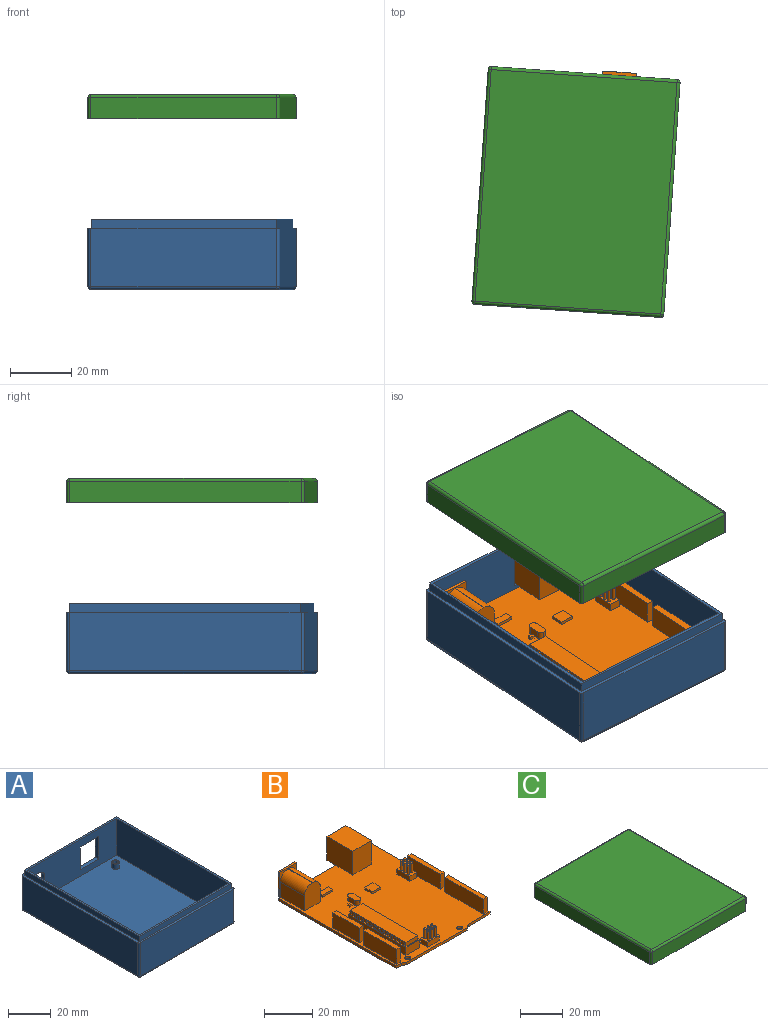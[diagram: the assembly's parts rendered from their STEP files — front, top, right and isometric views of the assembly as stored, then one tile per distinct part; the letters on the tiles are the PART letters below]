
ASSEMBLY  parts=3 mates=4
PART A: 49 faces, bbox 63x78x23 mm
  f0: plane 78x63mm, normal (0,0,1), area 294.3mm2, adj f2,f3,f4,f5,f32,f33,f34,f35
  f1: plane 59x21mm, normal (0,-1,0), area 1031.5mm2, adj f8,f9,f10,f27,f28,f29,f30,f31
  f2: plane 76x19mm, normal (1,0,0), area 1444mm2, adj f0,f39,f45,f48
  f3: plane 61x19mm, normal (0,-1,0), area 1159mm2, adj f0,f42,f46,f48
  f4: plane 76x19mm, normal (-1,0,0), area 1444mm2, adj f0,f37,f41,f42
  f5: plane 61x19mm, normal (0,1,0), area 951.5mm2, adj f0,f27,f28,f29,f30,f31,f37,f39
  f6: plane 76x61mm, normal (0,0,-1), area 4636mm2, adj f40,f41,f45,f46
  f7: plane 59x21mm, normal (0,1,0), area 1239mm2, adj f8,f9,f10,f36
  f8: plane 74x21mm, normal (-1,0,0), area 1554mm2, adj f1,f7,f10,f36
  f9: plane 74x21mm, normal (1,0,0), area 1554mm2, adj f1,f7,f10,f36
  f10: plane 74x59mm, normal (0,0,1), area 4327.5mm2, adj f1,f7,f8,f9,f12,f16,f20,f24
  f11: cylinder r=1.25mm len=3mm, axis (0,0,-1), area 23.6mm2, adj f13,f14
  f12: cylinder r=1.75mm len=3.5mm, axis (0,0,-1), area 33mm2, adj f10,f13
  f13: plane 3.5x3.5mm, normal (0,0,1), area 4.7mm2, adj f11,f12
  f14: plane 2.5x2.5mm, normal (0,0,1), area 4.9mm2, adj f11
  f15: cylinder r=1.25mm len=3mm, axis (0,0,-1), area 23.6mm2, adj f17,f18
  f16: cylinder r=1.75mm len=3.5mm, axis (0,0,-1), area 33mm2, adj f10,f17
  f17: plane 3.5x3.5mm, normal (0,0,1), area 4.7mm2, adj f15,f16
  f18: plane 2.5x2.5mm, normal (0,0,1), area 4.9mm2, adj f15
  f19: cylinder r=1.25mm len=3mm, axis (0,0,-1), area 23.6mm2, adj f21,f22
  f20: cylinder r=1.75mm len=3.5mm, axis (0,0,-1), area 33mm2, adj f10,f21
  f21: plane 3.5x3.5mm, normal (0,0,1), area 4.7mm2, adj f19,f20
  f22: plane 2.5x2.5mm, normal (0,0,1), area 4.9mm2, adj f19
  f23: cylinder r=1.25mm len=3mm, axis (0,0,-1), area 23.6mm2, adj f25,f26
  f24: cylinder r=1.75mm len=3.5mm, axis (0,0,-1), area 33mm2, adj f10,f25
  f25: plane 3.5x3.5mm, normal (0,0,1), area 4.7mm2, adj f23,f24
  f26: plane 2.5x2.5mm, normal (0,0,1), area 4.9mm2, adj f23
  f27: plane 13x2mm, normal (-1,0,0), area 26mm2, adj f1,f5,f28,f30
  f28: plane 12.11x2mm, normal (0,0,1), area 24.2mm2, adj f1,f5,f27,f29
  f29: plane 13x2mm, normal (1,0,0), area 26mm2, adj f1,f5,f28,f30
  f30: plane 12.11x2mm, normal (0,0,-1), area 24.2mm2, adj f1,f5,f27,f29
  f31: cylinder r=3.99mm len=7.98mm, axis (0,1,0), area 50.2mm2, adj f1,f5
  f32: plane 75.88x3mm, normal (1,0,0), area 227.6mm2, adj f0,f33,f35,f36
  f33: plane 60.88x3mm, normal (0,1,0), area 182.6mm2, adj f0,f32,f34,f36
  f34: plane 75.88x3mm, normal (-1,0,0), area 227.6mm2, adj f0,f33,f35,f36
  f35: plane 60.88x3mm, normal (0,-1,0), area 182.6mm2, adj f0,f32,f34,f36
  f36: plane 75.88x60.88mm, normal (0,0,1), area 252.9mm2, adj f1,f7,f8,f9,f32,f33,f34,f35
  f37: cylinder r=1mm len=19mm, axis (0,0,1), area 29.8mm2, adj f0,f4,f5,f38
  f38: sphere r=1mm, area 1.6mm2, adj f37,f40,f41
  f39: cylinder r=1mm len=19mm, axis (0,0,-1), area 29.8mm2, adj f0,f2,f5,f43
  f40: cylinder r=1mm len=61mm, axis (-1,0,0), area 95.8mm2, adj f5,f6,f38,f43
  f41: cylinder r=1mm len=76mm, axis (0,-1,0), area 119.4mm2, adj f4,f6,f38,f44
  f42: cylinder r=1mm len=19mm, axis (0,0,-1), area 29.8mm2, adj f0,f3,f4,f44
  f43: sphere r=1mm, area 1.6mm2, adj f39,f40,f45
  f44: sphere r=1mm, area 1.6mm2, adj f41,f42,f46
  f45: cylinder r=1mm len=76mm, axis (0,1,0), area 119.4mm2, adj f2,f6,f43,f47
  f46: cylinder r=1mm len=61mm, axis (1,0,0), area 95.8mm2, adj f3,f6,f44,f47
  f47: sphere r=1mm, area 1.6mm2, adj f45,f46,f48
  f48: cylinder r=1mm len=19mm, axis (0,0,1), area 29.8mm2, adj f0,f2,f3,f47
PART B: 244 faces, bbox 55x75.2x13.8 mm
  f0: plane 7x4mm, normal (0,0,1), area 23.3mm2, adj f194,f195,f196,f197,f226,f227,f228,f229
  f1: plane 7.5x4mm, normal (0,0,1), area 25.3mm2, adj f190,f191,f192,f193,f220,f221,f222,f223
  f2: plane 70x55mm, normal (0,0,1), area 3025.5mm2, adj f49,f50,f51,f52,f54,f55,f56,f57
  f3: plane 8.98x8.63mm, normal (0,1,0), area 52mm2, adj f179,f180,f181,f182,f183,f184,f185,f186
  f4: plane 1.5x0.4mm, normal (0,1,0), area 0.6mm2, adj f6,f46,f48,f178
  f5: plane 1.5x0.4mm, normal (0,-1,0), area 0.6mm2, adj f6,f46,f48,f178
  f6: plane 0.75x0.4mm, normal (0,0,1), area 0.3mm2, adj f4,f5,f46,f178
  f7: plane 1.5x0.4mm, normal (0,1,0), area 0.6mm2, adj f9,f46,f48,f177
  f8: plane 1.5x0.4mm, normal (0,-1,0), area 0.6mm2, adj f9,f46,f48,f177
  f9: plane 0.75x0.4mm, normal (0,0,1), area 0.3mm2, adj f7,f8,f46,f177
  f10: plane 1.5x0.4mm, normal (0,1,0), area 0.6mm2, adj f12,f46,f48,f176
  f11: plane 1.5x0.4mm, normal (0,-1,0), area 0.6mm2, adj f12,f46,f48,f176
  f12: plane 0.75x0.4mm, normal (0,0,1), area 0.3mm2, adj f10,f11,f46,f176
  f13: plane 1.5x0.4mm, normal (0,1,0), area 0.6mm2, adj f15,f46,f48,f175
  f14: plane 1.5x0.4mm, normal (0,-1,0), area 0.6mm2, adj f15,f46,f48,f175
  f15: plane 0.75x0.4mm, normal (0,0,1), area 0.3mm2, adj f13,f14,f46,f175
  f16: plane 1.5x0.4mm, normal (0,1,0), area 0.6mm2, adj f18,f46,f48,f174
  f17: plane 1.5x0.4mm, normal (0,-1,0), area 0.6mm2, adj f18,f46,f48,f174
  f18: plane 0.75x0.4mm, normal (0,0,1), area 0.3mm2, adj f16,f17,f46,f174
  f19: plane 1.5x0.4mm, normal (0,1,0), area 0.6mm2, adj f21,f46,f48,f173
  f20: plane 1.5x0.4mm, normal (0,-1,0), area 0.6mm2, adj f21,f46,f48,f173
  f21: plane 0.75x0.4mm, normal (0,0,1), area 0.3mm2, adj f19,f20,f46,f173
  f22: plane 1.5x0.4mm, normal (0,1,0), area 0.6mm2, adj f24,f46,f48,f172
  f23: plane 1.5x0.4mm, normal (0,-1,0), area 0.6mm2, adj f24,f46,f48,f172
  f24: plane 0.75x0.4mm, normal (0,0,1), area 0.3mm2, adj f22,f23,f46,f172
  f25: plane 1.5x0.4mm, normal (0,1,0), area 0.6mm2, adj f27,f46,f48,f171
  f26: plane 1.5x0.4mm, normal (0,-1,0), area 0.6mm2, adj f27,f46,f48,f171
  f27: plane 0.75x0.4mm, normal (0,0,1), area 0.3mm2, adj f25,f26,f46,f171
  f28: plane 1.5x0.4mm, normal (0,1,0), area 0.6mm2, adj f30,f46,f48,f170
  f29: plane 1.5x0.4mm, normal (0,-1,0), area 0.6mm2, adj f30,f46,f48,f170
  f30: plane 0.75x0.4mm, normal (0,0,1), area 0.3mm2, adj f28,f29,f46,f170
  f31: plane 1.5x0.4mm, normal (0,1,0), area 0.6mm2, adj f33,f46,f48,f169
  f32: plane 1.5x0.4mm, normal (0,-1,0), area 0.6mm2, adj f33,f46,f48,f169
  f33: plane 0.75x0.4mm, normal (0,0,1), area 0.3mm2, adj f31,f32,f46,f169
  f34: plane 1.5x0.4mm, normal (0,1,0), area 0.6mm2, adj f36,f46,f48,f168
  f35: plane 1.5x0.4mm, normal (0,-1,0), area 0.6mm2, adj f36,f46,f48,f168
  f36: plane 0.75x0.4mm, normal (0,0,1), area 0.3mm2, adj f34,f35,f46,f168
  f37: plane 1.5x0.4mm, normal (0,1,0), area 0.6mm2, adj f39,f46,f48,f167
  f38: plane 1.5x0.4mm, normal (0,-1,0), area 0.6mm2, adj f39,f46,f48,f167
  f39: plane 0.75x0.4mm, normal (0,0,1), area 0.3mm2, adj f37,f38,f46,f167
  f40: plane 1.5x0.4mm, normal (0,1,0), area 0.6mm2, adj f42,f46,f48,f166
  f41: plane 1.5x0.4mm, normal (0,-1,0), area 0.6mm2, adj f42,f46,f48,f166
  f42: plane 0.75x0.4mm, normal (0,0,1), area 0.3mm2, adj f40,f41,f46,f166
  f43: plane 1.5x0.4mm, normal (0,1,0), area 0.6mm2, adj f45,f46,f48,f165
  f44: plane 1.5x0.4mm, normal (0,-1,0), area 0.6mm2, adj f45,f46,f48,f165
  f45: plane 0.75x0.4mm, normal (0,0,1), area 0.3mm2, adj f43,f44,f46,f165
  f46: plane 32.63x2mm, normal (1,0,0), area 49.5mm2, adj f4,f5,f6,f7,f8,f9,f10,f11
  f47: plane 32.63x2mm, normal (-1,0,0), area 49.5mm2, adj f48,f106,f107,f108,f109,f110,f111,f112
  f48: plane 33.63x7.95mm, normal (0,0,1), area 32.2mm2, adj f4,f5,f7,f8,f10,f11,f13,f14
  f49: plane 33.63x4mm, normal (-1,0,0), area 134.5mm2, adj f2,f48,f50,f52
  f50: plane 7.95x4mm, normal (0,-1,0), area 31.8mm2, adj f2,f48,f49,f51
  f51: plane 33.63x4mm, normal (1,0,0), area 134.5mm2, adj f2,f48,f50,f52
  f52: plane 7.95x4mm, normal (0,1,0), area 31.8mm2, adj f2,f48,f49,f51
  f53: plane 6.98x6.98mm, normal (0,1,0), area 37.5mm2, adj f103,f104
  f54: plane 68.67x1.25mm, normal (1,0,0), area 85.8mm2, adj f2,f55,f58,f95
  f55: plane 55x1.25mm, normal (0,1,0), area 68.8mm2, adj f2,f54,f56,f58,f79,f84
  f56: plane 68.67x1.25mm, normal (-1,0,0), area 85.8mm2, adj f2,f55,f58,f92
  f57: plane 35.3x1.25mm, normal (0,-1,0), area 44.1mm2, adj f2,f58,f93,f94
  f58: plane 70x55mm, normal (0,0,-1), area 3816.6mm2, adj f54,f55,f56,f57,f92,f93,f94,f95
  f59: plane 7.5x2.22mm, normal (0,-1,0), area 16.7mm2, adj f2,f60,f62,f63
  f60: plane 22.58x7.5mm, normal (1,0,0), area 169.3mm2, adj f2,f59,f61,f63
  f61: plane 7.5x2.22mm, normal (0,1,0), area 16.7mm2, adj f2,f60,f62,f63
  f62: plane 22.58x7.5mm, normal (-1,0,0), area 169.3mm2, adj f2,f59,f61,f63
  f63: plane 22.58x2.22mm, normal (0,0,1), area 50.1mm2, adj f59,f60,f61,f62
  f64: plane 19.27x7.5mm, normal (-1,0,0), area 144.5mm2, adj f2,f65,f67,f68
  f65: plane 7.5x2.22mm, normal (0,-1,0), area 16.7mm2, adj f2,f64,f66,f68
  f66: plane 19.27x7.5mm, normal (1,0,0), area 144.5mm2, adj f2,f65,f67,f68
  f67: plane 7.5x2.22mm, normal (0,1,0), area 16.7mm2, adj f2,f64,f66,f68
  f68: plane 19.27x2.22mm, normal (0,0,1), area 42.8mm2, adj f64,f65,f66,f67
  f69: plane 19.1x7.5mm, normal (-1,0,0), area 143.2mm2, adj f2,f70,f72,f73
  f70: plane 7.5x2.22mm, normal (0,-1,0), area 16.7mm2, adj f2,f69,f71,f73
  f71: plane 19.1x7.5mm, normal (1,0,0), area 143.2mm2, adj f2,f70,f72,f73
  f72: plane 7.5x2.22mm, normal (0,1,0), area 16.7mm2, adj f2,f69,f71,f73
  f73: plane 19.1x2.22mm, normal (0,0,1), area 42.4mm2, adj f69,f70,f71,f72
  f74: plane 15.53x7.5mm, normal (1,0,0), area 116.5mm2, adj f2,f75,f77,f78
  f75: plane 7.5x2.22mm, normal (0,1,0), area 16.7mm2, adj f2,f74,f76,f78
  f76: plane 15.53x7.5mm, normal (-1,0,0), area 116.5mm2, adj f2,f75,f77,f78
  f77: plane 7.5x2.22mm, normal (0,-1,0), area 16.7mm2, adj f2,f74,f76,f78
  f78: plane 15.53x2.22mm, normal (0,0,1), area 34.5mm2, adj f74,f75,f76,f77
  f79: plane 9.89x1.2mm, normal (0,0,-1), area 11.7mm2, adj f55,f80,f82,f98,f99,f101,f102
  f80: plane 14.15x7.5mm, normal (-1,0,0), area 106.1mm2, adj f2,f79,f81,f90,f98
  f81: plane 12x9.24mm, normal (0,-1,0), area 102.2mm2, adj f2,f80,f82,f83,f90,f91
  f82: plane 14.15x7.5mm, normal (1,0,0), area 106.1mm2, adj f2,f79,f81,f91,f98
  f83: plane 14.15x0.24mm, normal (0,0,1), area 3.4mm2, adj f81,f90,f91,f98
  f84: plane 11.11x5.16mm, normal (0,0,-1), area 57.3mm2, adj f55,f85,f87,f88
  f85: plane 15.05x12mm, normal (-1,0,0), area 180.6mm2, adj f2,f84,f86,f88,f89
  f86: plane 12x11.11mm, normal (0,-1,0), area 133.3mm2, adj f2,f85,f87,f89
  f87: plane 15.05x12mm, normal (1,0,0), area 180.6mm2, adj f2,f84,f86,f88,f89
  f88: plane 12x11.11mm, normal (0,1,0), area 60.1mm2, adj f84,f85,f87,f89,f179,f180,f181,f182
  f89: plane 15.05x11.11mm, normal (0,0,1), area 167.2mm2, adj f85,f86,f87,f88
  f90: cylinder r=4.5mm len=14.15mm, axis (0,1,0), area 100mm2, adj f80,f81,f83,f98
  f91: cylinder r=4.5mm len=14.15mm, axis (0,-1,0), area 100mm2, adj f81,f82,f83,f98
  f92: plane 2.98x1.25mm, normal (0,-1,0), area 3.7mm2, adj f2,f56,f58,f93
  f93: plane 2.01x1.33mm, normal (-0.55,-0.83,0), area 3mm2, adj f2,f57,f58,f92
  f94: plane 2.01x1.33mm, normal (0.55,-0.83,0), area 3mm2, adj f2,f57,f58,f95
  f95: plane 12.71x1.25mm, normal (0,-1,0), area 15.9mm2, adj f2,f54,f58,f94
  f96: cylinder r=1.25mm len=2.5mm, axis (0,0,1), area 9.8mm2, adj f2,f58
  f97: cylinder r=1.25mm len=2.5mm, axis (0,0,1), area 9.8mm2, adj f2,f58
  f98: plane 12.57x9.89mm, normal (0,-1,0), area 22.1mm2, adj f79,f80,f82,f83,f90,f91,f99,f100
  f99: plane 12.57x1mm, normal (-1,0,0), area 12.6mm2, adj f79,f98,f100,f102
  f100: plane 9.89x1mm, normal (0,0,1), area 9.9mm2, adj f98,f99,f101,f102
  f101: plane 12.57x1mm, normal (1,0,0), area 12.6mm2, adj f79,f98,f100,f102
  f102: plane 12.57x9.89mm, normal (0,1,0), area 86mm2, adj f79,f99,f100,f101,f103
  f103: cylinder r=3.49mm len=12mm, axis (0,1,0), area 263.3mm2, adj f53,f102
  f104: cylinder r=0.5mm len=8mm, axis (0,-1,0), area 25.1mm2, adj f53,f105
  f105: plane 1x1mm, normal (0,1,0), area 0.8mm2, adj f104
  f106: plane 6.95x2mm, normal (0,1,0), area 13.9mm2, adj f46,f47,f48,f108
  f107: plane 6.95x2mm, normal (0,-1,0), area 13.9mm2, adj f46,f47,f48,f108
  f108: plane 32.63x6.95mm, normal (0,0,1), area 226.7mm2, adj f46,f47,f106,f107
  f109: plane 1.5x0.4mm, normal (0,1,0), area 0.6mm2, adj f47,f48,f111,f164
  f110: plane 1.5x0.4mm, normal (0,-1,0), area 0.6mm2, adj f47,f48,f111,f164
  f111: plane 0.75x0.4mm, normal (0,0,1), area 0.3mm2, adj f47,f109,f110,f164
  f112: plane 1.5x0.4mm, normal (0,1,0), area 0.6mm2, adj f47,f48,f114,f163
  f113: plane 1.5x0.4mm, normal (0,-1,0), area 0.6mm2, adj f47,f48,f114,f163
  f114: plane 0.75x0.4mm, normal (0,0,1), area 0.3mm2, adj f47,f112,f113,f163
  f115: plane 1.5x0.4mm, normal (0,1,0), area 0.6mm2, adj f47,f48,f117,f162
  f116: plane 1.5x0.4mm, normal (0,-1,0), area 0.6mm2, adj f47,f48,f117,f162
  f117: plane 0.75x0.4mm, normal (0,0,1), area 0.3mm2, adj f47,f115,f116,f162
  f118: plane 1.5x0.4mm, normal (0,1,0), area 0.6mm2, adj f47,f48,f120,f161
  f119: plane 1.5x0.4mm, normal (0,-1,0), area 0.6mm2, adj f47,f48,f120,f161
  f120: plane 0.75x0.4mm, normal (0,0,1), area 0.3mm2, adj f47,f118,f119,f161
  f121: plane 1.5x0.4mm, normal (0,1,0), area 0.6mm2, adj f47,f48,f123,f160
  f122: plane 1.5x0.4mm, normal (0,-1,0), area 0.6mm2, adj f47,f48,f123,f160
  f123: plane 0.75x0.4mm, normal (0,0,1), area 0.3mm2, adj f47,f121,f122,f160
  f124: plane 1.5x0.4mm, normal (0,1,0), area 0.6mm2, adj f47,f48,f126,f159
  f125: plane 1.5x0.4mm, normal (0,-1,0), area 0.6mm2, adj f47,f48,f126,f159
  f126: plane 0.75x0.4mm, normal (0,0,1), area 0.3mm2, adj f47,f124,f125,f159
  f127: plane 1.5x0.4mm, normal (0,1,0), area 0.6mm2, adj f47,f48,f129,f158
  f128: plane 1.5x0.4mm, normal (0,-1,0), area 0.6mm2, adj f47,f48,f129,f158
  f129: plane 0.75x0.4mm, normal (0,0,1), area 0.3mm2, adj f47,f127,f128,f158
  f130: plane 1.5x0.4mm, normal (0,1,0), area 0.6mm2, adj f47,f48,f132,f157
  f131: plane 1.5x0.4mm, normal (0,-1,0), area 0.6mm2, adj f47,f48,f132,f157
  f132: plane 0.75x0.4mm, normal (0,0,1), area 0.3mm2, adj f47,f130,f131,f157
  f133: plane 1.5x0.4mm, normal (0,1,0), area 0.6mm2, adj f47,f48,f135,f156
  f134: plane 1.5x0.4mm, normal (0,-1,0), area 0.6mm2, adj f47,f48,f135,f156
  f135: plane 0.75x0.4mm, normal (0,0,1), area 0.3mm2, adj f47,f133,f134,f156
  f136: plane 1.5x0.4mm, normal (0,1,0), area 0.6mm2, adj f47,f48,f138,f155
  f137: plane 1.5x0.4mm, normal (0,-1,0), area 0.6mm2, adj f47,f48,f138,f155
  f138: plane 0.75x0.4mm, normal (0,0,1), area 0.3mm2, adj f47,f136,f137,f155
  f139: plane 1.5x0.4mm, normal (0,1,0), area 0.6mm2, adj f47,f48,f141,f154
  f140: plane 1.5x0.4mm, normal (0,-1,0), area 0.6mm2, adj f47,f48,f141,f154
  f141: plane 0.75x0.4mm, normal (0,0,1), area 0.3mm2, adj f47,f139,f140,f154
  f142: plane 1.5x0.4mm, normal (0,1,0), area 0.6mm2, adj f47,f48,f144,f153
  f143: plane 1.5x0.4mm, normal (0,-1,0), area 0.6mm2, adj f47,f48,f144,f153
  f144: plane 0.75x0.4mm, normal (0,0,1), area 0.3mm2, adj f47,f142,f143,f153
  f145: plane 1.5x0.4mm, normal (0,1,0), area 0.6mm2, adj f47,f48,f147,f152
  f146: plane 1.5x0.4mm, normal (0,-1,0), area 0.6mm2, adj f47,f48,f147,f152
  f147: plane 0.75x0.4mm, normal (0,0,1), area 0.3mm2, adj f47,f145,f146,f152
  f148: plane 1.5x0.4mm, normal (0,1,0), area 0.6mm2, adj f47,f48,f150,f151
  f149: plane 1.5x0.4mm, normal (0,-1,0), area 0.6mm2, adj f47,f48,f150,f151
  f150: plane 0.75x0.4mm, normal (0,0,1), area 0.3mm2, adj f47,f148,f149,f151
  f151: plane 1.5x0.75mm, normal (-1,0,0), area 1.1mm2, adj f48,f148,f149,f150
  f152: plane 1.5x0.75mm, normal (-1,0,0), area 1.1mm2, adj f48,f145,f146,f147
  f153: plane 1.5x0.75mm, normal (-1,0,0), area 1.1mm2, adj f48,f142,f143,f144
  f154: plane 1.5x0.75mm, normal (-1,0,0), area 1.1mm2, adj f48,f139,f140,f141
  f155: plane 1.5x0.75mm, normal (-1,0,0), area 1.1mm2, adj f48,f136,f137,f138
  f156: plane 1.5x0.75mm, normal (-1,0,0), area 1.1mm2, adj f48,f133,f134,f135
  f157: plane 1.5x0.75mm, normal (-1,0,0), area 1.1mm2, adj f48,f130,f131,f132
  f158: plane 1.5x0.75mm, normal (-1,0,0), area 1.1mm2, adj f48,f127,f128,f129
  f159: plane 1.5x0.75mm, normal (-1,0,0), area 1.1mm2, adj f48,f124,f125,f126
  f160: plane 1.5x0.75mm, normal (-1,0,0), area 1.1mm2, adj f48,f121,f122,f123
  f161: plane 1.5x0.75mm, normal (-1,0,0), area 1.1mm2, adj f48,f118,f119,f120
  f162: plane 1.5x0.75mm, normal (-1,0,0), area 1.1mm2, adj f48,f115,f116,f117
  f163: plane 1.5x0.75mm, normal (-1,0,0), area 1.1mm2, adj f48,f112,f113,f114
  f164: plane 1.5x0.75mm, normal (-1,0,0), area 1.1mm2, adj f48,f109,f110,f111
  f165: plane 1.5x0.75mm, normal (1,0,0), area 1.1mm2, adj f43,f44,f45,f48
  f166: plane 1.5x0.75mm, normal (1,0,0), area 1.1mm2, adj f40,f41,f42,f48
  f167: plane 1.5x0.75mm, normal (1,0,0), area 1.1mm2, adj f37,f38,f39,f48
  f168: plane 1.5x0.75mm, normal (1,0,0), area 1.1mm2, adj f34,f35,f36,f48
  f169: plane 1.5x0.75mm, normal (1,0,0), area 1.1mm2, adj f31,f32,f33,f48
  f170: plane 1.5x0.75mm, normal (1,0,0), area 1.1mm2, adj f28,f29,f30,f48
  f171: plane 1.5x0.75mm, normal (1,0,0), area 1.1mm2, adj f25,f26,f27,f48
  f172: plane 1.5x0.75mm, normal (1,0,0), area 1.1mm2, adj f22,f23,f24,f48
  f173: plane 1.5x0.75mm, normal (1,0,0), area 1.1mm2, adj f19,f20,f21,f48
  f174: plane 1.5x0.75mm, normal (1,0,0), area 1.1mm2, adj f16,f17,f18,f48
  f175: plane 1.5x0.75mm, normal (1,0,0), area 1.1mm2, adj f13,f14,f15,f48
  f176: plane 1.5x0.75mm, normal (1,0,0), area 1.1mm2, adj f10,f11,f12,f48
  f177: plane 1.5x0.75mm, normal (1,0,0), area 1.1mm2, adj f7,f8,f9,f48
  f178: plane 1.5x0.75mm, normal (1,0,0), area 1.1mm2, adj f4,f5,f6,f48
  f179: plane 10x6.73mm, normal (1,0,0), area 67.3mm2, adj f3,f88,f180,f184
  f180: plane 10x8.63mm, normal (0,0,1), area 86.3mm2, adj f3,f88,f179,f181
  f181: plane 10x6.73mm, normal (-1,0,0), area 67.3mm2, adj f3,f88,f180,f182
  f182: plane 10x2.24mm, normal (-0.76,0,-0.65), area 29.4mm2, adj f3,f88,f181,f183
  f183: plane 10x4.83mm, normal (0,0,-1), area 48.3mm2, adj f3,f88,f182,f184
  f184: plane 10x2.24mm, normal (0.76,0,-0.65), area 29.4mm2, adj f3,f88,f179,f183
  f185: plane 8x3.45mm, normal (-1,0,0), area 27.6mm2, adj f3,f186,f188,f189
  f186: plane 8x6.13mm, normal (0,0,1), area 49mm2, adj f3,f185,f187,f189
  f187: plane 8x3.45mm, normal (1,0,0), area 27.6mm2, adj f3,f186,f188,f189
  f188: plane 8x6.13mm, normal (0,0,-1), area 49mm2, adj f3,f185,f187,f189
  f189: plane 6.13x3.45mm, normal (0,1,0), area 21.2mm2, adj f185,f186,f187,f188
  f190: plane 7.5x2.5mm, normal (-1,0,0), area 18.7mm2, adj f1,f2,f191,f193
  f191: plane 4x2.5mm, normal (0,-1,0), area 10mm2, adj f1,f2,f190,f192
  f192: plane 7.5x2.5mm, normal (1,0,0), area 18.7mm2, adj f1,f2,f191,f193
  f193: plane 4x2.5mm, normal (0,1,0), area 10mm2, adj f1,f2,f190,f192
  f194: plane 4x2.5mm, normal (-1,0,0), area 10mm2, adj f0,f2,f195,f197
  f195: plane 7x2.5mm, normal (0,-1,0), area 17.5mm2, adj f0,f2,f194,f196
  f196: plane 4x2.5mm, normal (1,0,0), area 10mm2, adj f0,f2,f195,f197
  f197: plane 7x2.5mm, normal (0,1,0), area 17.5mm2, adj f0,f2,f194,f196
  f198: plane 3.5x2.5mm, normal (-1,0,0), area 8.8mm2, adj f2,f200,f201,f203
  f199: plane 3.5x2.5mm, normal (1,0,0), area 8.8mm2, adj f2,f200,f202,f204
  f200: plane 6.5x3mm, normal (0,0,1), area 17.6mm2, adj f198,f199,f201,f202,f203,f204
  f201: cylinder r=1.5mm len=2.5mm, axis (0,0,-1), area 5.9mm2, adj f2,f198,f200,f202
  f202: cylinder r=1.5mm len=2.5mm, axis (0,0,-1), area 5.9mm2, adj f2,f199,f200,f201
  f203: cylinder r=1.5mm len=2.5mm, axis (0,0,-1), area 5.9mm2, adj f2,f198,f200,f204
  f204: cylinder r=1.5mm len=2.5mm, axis (0,0,-1), area 5.9mm2, adj f2,f199,f200,f203
  f205: plane 2.66x1mm, normal (-1,0,0), area 2.7mm2, adj f2,f206,f208,f209
  f206: plane 5.95x1mm, normal (0,-1,0), area 6mm2, adj f2,f205,f207,f209
  f207: plane 2.66x1mm, normal (1,0,0), area 2.7mm2, adj f2,f206,f208,f209
  f208: plane 5.95x1mm, normal (0,1,0), area 6mm2, adj f2,f205,f207,f209
  f209: plane 5.95x2.66mm, normal (0,0,1), area 15.9mm2, adj f205,f206,f207,f208
  f210: plane 1.1x1mm, normal (-1,0,0), area 1.1mm2, adj f2,f211,f213,f214
  f211: plane 1.57x1mm, normal (0,-1,0), area 1.6mm2, adj f2,f210,f212,f214
  f212: plane 1.1x1mm, normal (1,0,0), area 1.1mm2, adj f2,f211,f213,f214
  f213: plane 1.57x1mm, normal (0,1,0), area 1.6mm2, adj f2,f210,f212,f214
  f214: plane 1.57x1.1mm, normal (0,0,1), area 1.7mm2, adj f210,f211,f212,f213
  f215: plane 4.54x1mm, normal (-1,0,0), area 4.5mm2, adj f2,f216,f218,f219
  f216: plane 4.86x1mm, normal (0,-1,0), area 4.9mm2, adj f2,f215,f217,f219
  f217: plane 4.54x1mm, normal (1,0,0), area 4.5mm2, adj f2,f216,f218,f219
  f218: plane 4.86x1mm, normal (0,1,0), area 4.9mm2, adj f2,f215,f217,f219
  f219: plane 4.86x4.54mm, normal (0,0,1), area 22.1mm2, adj f215,f216,f217,f218
  f220: cylinder r=0.5mm len=4.5mm, axis (0,0,-1), area 14.1mm2, adj f1,f237
  f221: cylinder r=0.5mm len=4.5mm, axis (0,0,-1), area 14.1mm2, adj f1,f238
  f222: cylinder r=0.5mm len=4.5mm, axis (0,0,-1), area 14.1mm2, adj f1,f235
  f223: cylinder r=0.5mm len=4.5mm, axis (0,0,-1), area 14.1mm2, adj f1,f232
  f224: cylinder r=0.5mm len=4.5mm, axis (0,0,-1), area 14.1mm2, adj f1,f233
  f225: cylinder r=0.5mm len=4.5mm, axis (0,0,-1), area 14.1mm2, adj f1,f234
  f226: cylinder r=0.5mm len=4.5mm, axis (0,0,-1), area 14.1mm2, adj f0,f239
  f227: cylinder r=0.5mm len=4.5mm, axis (0,0,-1), area 14.1mm2, adj f0,f236
  f228: cylinder r=0.5mm len=4.5mm, axis (0,0,-1), area 14.1mm2, adj f0,f242
  f229: cylinder r=0.5mm len=4.5mm, axis (0,0,-1), area 14.1mm2, adj f0,f241
  f230: cylinder r=0.5mm len=4.5mm, axis (0,0,-1), area 14.1mm2, adj f0,f240
  f231: cylinder r=0.5mm len=4.5mm, axis (0,0,-1), area 14.1mm2, adj f0,f243
  f232: sphere r=0.5mm, area 1.6mm2, adj f223
  f233: sphere r=0.5mm, area 1.6mm2, adj f224
  f234: sphere r=0.5mm, area 1.6mm2, adj f225
  f235: sphere r=0.5mm, area 1.6mm2, adj f222
  f236: sphere r=0.5mm, area 1.6mm2, adj f227
  f237: sphere r=0.5mm, area 1.6mm2, adj f220
  f238: sphere r=0.5mm, area 1.6mm2, adj f221
  f239: sphere r=0.5mm, area 1.6mm2, adj f226
  f240: sphere r=0.5mm, area 1.6mm2, adj f230
  f241: sphere r=0.5mm, area 1.6mm2, adj f229
  f242: sphere r=0.5mm, area 1.6mm2, adj f228
  f243: sphere r=0.5mm, area 1.6mm2, adj f231
PART C: 28 faces, bbox 63x78x8 mm
  f0: plane 78x63mm, normal (0,0,-1), area 294.3mm2, adj f1,f2,f3,f4,f6,f7,f8,f9
  f1: plane 76x7mm, normal (1,0,0), area 532mm2, adj f0,f18,f24,f27
  f2: plane 61x7mm, normal (0,1,0), area 427mm2, adj f0,f21,f25,f27
  f3: plane 76x7mm, normal (-1,0,0), area 532mm2, adj f0,f16,f20,f21
  f4: plane 61x7mm, normal (0,-1,0), area 427mm2, adj f0,f16,f18,f19
  f5: plane 76x61mm, normal (0,0,1), area 4636mm2, adj f19,f20,f24,f25
  f6: plane 75.88x3mm, normal (-1,0,0), area 227.6mm2, adj f0,f7,f9,f10
  f7: plane 60.88x3mm, normal (0,-1,0), area 182.6mm2, adj f0,f6,f8,f10
  f8: plane 75.88x3mm, normal (1,0,0), area 227.6mm2, adj f0,f7,f9,f10
  f9: plane 60.88x3mm, normal (0,1,0), area 182.6mm2, adj f0,f6,f8,f10
  f10: plane 75.88x60.88mm, normal (0,0,-1), area 252.9mm2, adj f6,f7,f8,f9,f12,f13,f14,f15
  f11: plane 74x59mm, normal (0,0,-1), area 4366mm2, adj f12,f13,f14,f15
  f12: plane 74x3mm, normal (1,0,0), area 222mm2, adj f10,f11,f13,f15
  f13: plane 59x3mm, normal (0,-1,0), area 177mm2, adj f10,f11,f12,f14
  f14: plane 74x3mm, normal (-1,0,0), area 222mm2, adj f10,f11,f13,f15
  f15: plane 59x3mm, normal (0,1,0), area 177mm2, adj f10,f11,f12,f14
  f16: cylinder r=1mm len=7mm, axis (0,0,1), area 11mm2, adj f0,f3,f4,f17
  f17: sphere r=1mm, area 1.6mm2, adj f16,f19,f20
  f18: cylinder r=1mm len=7mm, axis (0,0,-1), area 11mm2, adj f0,f1,f4,f22
  f19: cylinder r=1mm len=61mm, axis (-1,0,0), area 95.8mm2, adj f4,f5,f17,f22
  f20: cylinder r=1mm len=76mm, axis (0,1,0), area 119.4mm2, adj f3,f5,f17,f23
  f21: cylinder r=1mm len=7mm, axis (0,0,-1), area 11mm2, adj f0,f2,f3,f23
  f22: sphere r=1mm, area 1.6mm2, adj f18,f19,f24
  f23: sphere r=1mm, area 1.6mm2, adj f20,f21,f25
  f24: cylinder r=1mm len=76mm, axis (0,-1,0), area 119.4mm2, adj f1,f5,f22,f26
  f25: cylinder r=1mm len=61mm, axis (1,0,0), area 95.8mm2, adj f2,f5,f23,f26
  f26: sphere r=1mm, area 1.6mm2, adj f24,f25,f27
  f27: cylinder r=1mm len=7mm, axis (0,0,1), area 11mm2, adj f0,f1,f2,f26
PLACE A rot(axis=(0,0,-1),4deg) t=(-40.8,-55.1,23.35)mm fixed
PLACE B rot(axis=(0,0,-1),4deg) t=(-40.8,-55.1,23.35)mm
PLACE C rot(axis=(0,0,-1),4deg) t=(-40.8,-55.1,59.24)mm
MATE planar C.f6 <-> A.f32  axis (-1,0.07,0) through (-10.41,-57.19,75.74)mm
MATE cylindrical A.f15 <-> B.f96  axis (0,0,1) through (-63.06,-86.62,23.35)mm
MATE planar C.f9 <-> A.f35  axis (0.07,1,0) through (-43.42,-92.91,75.74)mm
MATE planar B.f58 <-> A.f11  axis (0,0,-1) through (-40.84,-54.8,23.35)mm
